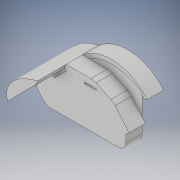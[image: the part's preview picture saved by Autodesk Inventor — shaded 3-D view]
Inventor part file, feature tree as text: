
AUTODESK INVENTOR PART (.ipt)
format: ipt  version: 2017 (Build 210142000, 142)  size: 602,112 bytes
history: native  units: mm
features: sketch x30, extrude x26, plane x7, other x3, fillet x3, revolve x1, boolean_combine x1
ambient origin geometry x8: Origin, YZ Plane, XZ Plane, XY Plane, X Axis, Y Axis, Z Axis, Center Point
bodies: Solid1 (feature_tree), Solid2 (feature_tree)
feature tree (71):
  extrude  "Extrusion1"  Depth=60.0mm
  plane  "Work Plane1"
  extrude  "Extrusion2"  Depth=60.0mm
  other  "Bend Part1"
  other  "Bend Part2"
  extrude  "Extrusion3"  Depth=32.454mm
  plane  "Work Plane2"
  extrude  "Extrusion4"  Depth=20.0mm
  other  "Bend Part3"
  extrude  "Extrusion5"  Depth=30.0mm
  revolve  "Revolution1"  [1 undecoded]
  plane  "Work Plane3"
  extrude  "Extrusion6"  Depth=10.0mm
  boolean_combine  "Combine1"
  plane  "Work Plane4"
  extrude  "Extrusion7"  TaperAngle=90.0deg  [1 undecoded]
  extrude  "Extrusion8"  Depth=80.0mm
  extrude  "Extrusion9"  Depth=50.0mm TaperAngle=135.0deg
  extrude  "Extrusion10"  Depth=60.0mm
  plane  "Work Plane5"
  extrude  "Extrusion11"  Depth=60.0mm
  extrude  "Extrusion12"  Depth=60.0mm
  plane  "Work Plane6"
  extrude  "Extrusion13"  [1 undecoded]
  extrude  "Extrusion14"  Depth=30.0mm TaperAngle=0.0deg
  plane  "Work Plane7"
  extrude  "Extrusion15"  Depth=20.0mm TaperAngle=0.0deg
  extrude  "Extrusion16"  Depth=15.219936mm
  extrude  "Extrusion17"  Depth=15.155142mm
  fillet  "Fillet1"  Radius=20.0mm
  extrude  "Extrusion18"  Depth=60.0mm
  fillet  "Fillet2"  Radius=43.193283mm
  fillet  "Fillet3"  Radius=60.0mm
  extrude  "Extrusion19"  Depth=14.497104mm
  extrude  "Extrusion20"  Depth=104.0mm TaperAngle=0.0deg
  extrude  "Extrusion21"  [1 undecoded]
  extrude  "Extrusion22"  Depth=1.164325mm
  extrude  "Extrusion23"  Depth=25.536883mm
  extrude  "Extrusion24"  TaperAngle=0.0deg  [1 undecoded]
  extrude  "Extrusion25"  Depth=50.209mm
  extrude  "Extrusion26"  Depth=95.197mm TaperAngle=0.0deg
  sketch  "Sketch1"  dims[d0=60.0mm d1=35.0mm]
  sketch  "Sketch2"  dims[d2=60.0mm d3=33.005006mm]
  sketch  "Sketch3"  dims[d4=75.0mm d5=0.0mm d6=32.454mm]
  sketch  "Sketch4"  dims[d7=85.0mm d8=20.0mm]
  sketch  "Sketch5"  dims[d9=5.0mm d10=0.0mm d11=30.0mm]
  sketch  "Sketch6"  dims[d12=55.0mm d13=10.0mm d14=4.363323mm]
  sketch  "Sketch7"  dims[d15=20.0mm d16=10.0mm d17=4.363323mm]
  sketch  "Sketch8"  dims[d18=20.0mm d19=0.0mm d20=90.0deg]
  sketch  "Sketch9"  dims[d21=20.0mm d22=80.0mm]
  sketch  "Sketch10"  dims[d23=5.0mm d24=0.0mm d25=50.0mm d26=135.0deg]
  sketch  "Sketch11"  dims[d27=60.0mm d28=35.0mm]
  sketch  "Sketch12"  dims[d29=35.0mm d30=60.0mm]
  sketch  "Sketch13"  dims[d31=20.0mm d32=0.0mm d33=60.0mm]
  sketch  "Sketch14"  dims[d34=270.0deg d35=-4.697mm]
  sketch  "Sketch15"  dims[d36=20.0mm d37=30.0mm d38=0.0mm]
  sketch  "Sketch16"  dims[d39=-20.0mm d40=20.0mm d41=0.0mm]
  sketch  "Sketch17"  dims[d42=35.67mm d43=15.219936mm]
  sketch  "Sketch18"  dims[d44=35.67mm d45=15.155142mm d46=20.0mm d47=0.0mm]
  sketch  "Sketch19"  dims[d48=20.0mm d49=0.0mm d50=100.334153mm d51=43.193283mm d52=60.0mm d53=0.0mm]
  sketch  "Sketch20"  dims[d54=60.5mm d55=14.497104mm]
  sketch  "Sketch21"  dims[d56=25.287025mm d57=104.0mm d58=0.0mm]
  sketch  "Sketch22"  dims[d59=2.439mm d60=0.0mm d61=-31.25mm]
  sketch  "Sketch23"  dims[d62=0.980484mm d63=1.164325mm]
  sketch  "Sketch24"  dims[d64=2.246206mm d65=25.536883mm]
  sketch  "Sketch25"  dims[d66=100.0mm d67=0.0mm d68=0.0mm]
  sketch  "Sketch26"  dims[d69=5.0mm d70=0.0mm d71=50.209mm]
  sketch  "Sketch27"  dims[d72=95.197mm d73=0.0mm d74=95.197mm d75=0.0mm]
  sketch  "Sketch28"  dims[d76=60.0mm]
  sketch  "Sketch29"  dims[d77=60.0mm]
  sketch  "Sketch30"  dims[d78=20.0mm d79=18.461mm d80=116.447mm d81=0.0mm d82=10.0mm d83=8.797686mm d84=116.447mm d85=0.0mm d86=10.0mm d87=9.0mm d89=60.197145mm d90=34.482005mm d91=20.0mm d92=3.0mm d93=20.0mm d94=90.0deg d95=55.512917mm d96=23.386841mm d97=11.976391mm d98=75.0mm d99=0.0mm d100=3.0mm d101=20.0mm d102=75.0mm d103=0.0mm d104=14.0mm d105=2.0mm d106=75.0mm d107=0.0mm d108=20.0mm d109=0.0mm d110=20.0mm d111=0.0mm d112=20.0mm d113=0.0mm d114=20.0mm d115=0.0mm d116=20.0mm d117=60.0mm d118=10.0mm d119=0.0mm]
note: 5 required parameter values undecoded (feature->parameter linkage not recoverable at this tier; creation-order binding heuristic only, values carry confidence <= 0.55)